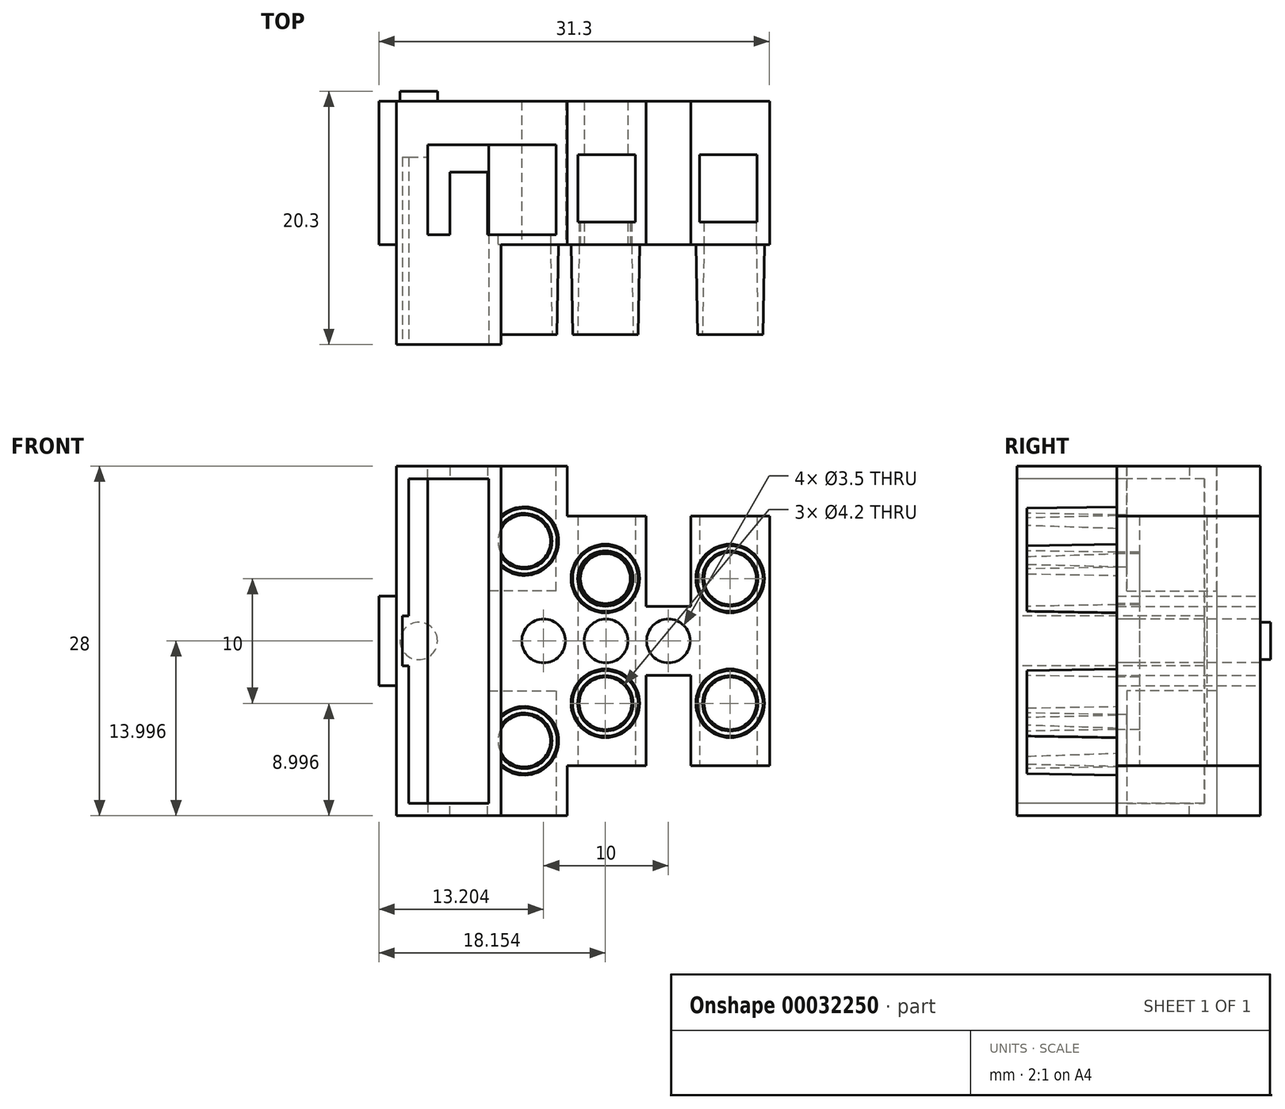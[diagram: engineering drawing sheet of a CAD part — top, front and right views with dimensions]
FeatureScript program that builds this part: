
annotation { "Feature Type Name" : "Feature", "Feature Type Description" : "" }
export const myFeature = defineFeature(function(context is Context, id is Id, definition is map)
    precondition{}
    {
        {
            var Q0;
            Q0=qCreatedBy(makeId("Front.planeOp"),FACE);
            var sketch = newSketch(context, id + "F0", { "sketchPlane" : qUnion([Q0])});
            skLineSegment(sketch, "E0", {"start": v(0.2, 10.65) * mm, "end": v(-6.1, 10.65) * mm});
            skLineSegment(sketch, "E1", {"start": v(-6.1, 10.65) * mm, "end": v(-6.1, 3.4) * mm});
            skLineSegment(sketch, "E2", {"start": v(-6.1, 3.4) * mm, "end": v(-9.7, 3.4) * mm});
            skLineSegment(sketch, "E3", {"start": v(-9.7, 3.4) * mm, "end": v(-9.7, 10.65) * mm});
            skLineSegment(sketch, "E4", {"start": v(-9.7, 10.65) * mm, "end": v(-16, 10.65) * mm});
            skLineSegment(sketch, "E5", {"start": v(0.2, -9.35) * mm, "end": v(-6.1, -9.35) * mm});
            skLineSegment(sketch, "E6", {"start": v(-6.1, -9.35) * mm, "end": v(-6.1, -2.1) * mm});
            skLineSegment(sketch, "E7", {"start": v(-6.1, -2.1) * mm, "end": v(-9.7, -2.1) * mm});
            skLineSegment(sketch, "E8", {"start": v(-9.7, -2.1) * mm, "end": v(-9.7, -9.35) * mm});
            skLineSegment(sketch, "E9", {"start": v(-9.7, -9.35) * mm, "end": v(-16, -9.35) * mm});
            skLineSegment(sketch, "E10", {"start": v(-16, 10.65) * mm, "end": v(-16, 14.65) * mm});
            skLineSegment(sketch, "E11", {"start": v(-16, 14.65) * mm, "end": v(-29.7, 14.65) * mm});
            skLineSegment(sketch, "E12", {"start": v(-29.7, 14.65) * mm, "end": v(-29.7, 4.25) * mm});
            skLineSegment(sketch, "E13", {"start": v(-29.7, -13.35) * mm, "end": v(-16, -13.35) * mm});
            skLineSegment(sketch, "E14", {"start": v(-16, -13.35) * mm, "end": v(-16, -9.35) * mm});
            skLineSegment(sketch, "E15", {"start": v(0.2, 10.65) * mm, "end": v(0.2, -9.35) * mm});
            skLineSegment(sketch, "E16", {"start": v(0.3, 0.65) * mm, "end": v(-43.59, 0.65) * mm, "construction": true});
            skLineSegment(sketch, "E17", {"start": v(-29.7, 4.25) * mm, "end": v(-31.1, 4.25) * mm});
            skLineSegment(sketch, "E18", {"start": v(-31.1, 4.25) * mm, "end": v(-31.1, -2.95) * mm});
            skLineSegment(sketch, "E19", {"start": v(-31.1, -2.95) * mm, "end": v(-29.7, -2.95) * mm});
            skLineSegment(sketch, "E20.trimOffspring", {"start": v(-29.7, -2.95) * mm, "end": v(-29.7, -13.35) * mm});
            skSolve(sketch);
        }
        {
            var Q0;
            Q0 = qSketchRegion(id + "F0", true);
            extrude(context, id + "F1", {"entities" : qUnion([Q0]), "depth" : 11.5 * mm});
        }
        {
            var Q0;
            Q0=makeQuery(id+"F1.opExtrude","CAP_FACE",FACE,{"disambiguationData":[OSD([sQuery(id+"F0.wireOp",EDGE,"E0"),sQuery(id+"F0.wireOp",EDGE,"E1"),sQuery(id+"F0.wireOp",EDGE,"E2"),sQuery(id+"F0.wireOp",EDGE,"E3"),sQuery(id+"F0.wireOp",EDGE,"E4"),sQuery(id+"F0.wireOp",EDGE,"E5"),sQuery(id+"F0.wireOp",EDGE,"E6"),sQuery(id+"F0.wireOp",EDGE,"E7"),sQuery(id+"F0.wireOp",EDGE,"E8"),sQuery(id+"F0.wireOp",EDGE,"E9"),sQuery(id+"F0.wireOp",EDGE,"E10"),sQuery(id+"F0.wireOp",EDGE,"E11"),sQuery(id+"F0.wireOp",EDGE,"E12"),sQuery(id+"F0.wireOp",EDGE,"E13"),sQuery(id+"F0.wireOp",EDGE,"E14"),sQuery(id+"F0.wireOp",EDGE,"E15")])],"isStart":false});
            var sketch = newSketch(context, id + "F2", { "sketchPlane" : qUnion([Q0])});
            skLineSegment(sketch, "E21", {"start": v(0.2, -0.45) * mm, "end": v(-41.93, -0.45) * mm, "construction": true});
            skSolve(sketch);
        }
        {
            var Q0;
            Q0=makeQuery(id+"F2.imprint","IMPRINT",FACE,{"disambiguationData":[TD([[makeQuery(id+"F2.imprint","IMPRINT",EDGE,{"derivedFrom":makeQuery(id+"F1.opExtrude","CAP_EDGE",EDGE,{"disambiguationData":[OSD([sQuery(id+"F0.wireOp",EDGE,"E0")])],"isStart":false})}),1.0]])]});
            var sketch = newSketch(context, id + "F3", { "sketchPlane" : qUnion([Q0])});
            skCircle(sketch, "E22", {"center": v(-2.96, 5.65) * mm, "radius": 2.1 * mm});
            skCircle(sketch, "E23", {"center": v(-2.96, -4.35) * mm, "radius": 2.1 * mm});
            skCircle(sketch, "E24", {"center": v(-12.96, 5.65) * mm, "radius": 2.1 * mm});
            skCircle(sketch, "E25", {"center": v(-12.96, -4.35) * mm, "radius": 2.1 * mm});
            skCircle(sketch, "E26", {"center": v(-19.46, 8.65) * mm, "radius": 2.1 * mm});
            skCircle(sketch, "E27", {"center": v(-19.46, -7.35) * mm, "radius": 2.1 * mm});
            skCircle(sketch, "E28", {"center": v(-2.96, 5.65) * mm, "radius": 2.75 * mm});
            skCircle(sketch, "E29", {"center": v(-2.96, -4.35) * mm, "radius": 2.75 * mm});
            skCircle(sketch, "E30", {"center": v(-12.96, 5.65) * mm, "radius": 2.75 * mm});
            skCircle(sketch, "E31", {"center": v(-12.96, -4.35) * mm, "radius": 2.75 * mm});
            skCircle(sketch, "E32", {"center": v(-19.46, -7.35) * mm, "radius": 2.75 * mm});
            skCircle(sketch, "E33", {"center": v(-19.46, 8.65) * mm, "radius": 2.75 * mm});
            skSolve(sketch);
        }
        {
            var Q0;
            Q0 = qSketchRegion(id + "F3", true);
            extrude(context, id + "F4", {"entities" : qUnion([Q0]), "operationType" : NewBodyOperationType.ADD, "depth" : 7.2 * mm, "hasDraft" : true, "draftAngle" : 1 * degree, "draftPullDirection" : true});
        }
        {
            var Q0;
            Q0=makeQuery(id+"F2.imprint","IMPRINT",FACE,{"disambiguationData":[TD([[makeQuery(id+"F2.imprint","IMPRINT",EDGE,{"derivedFrom":makeQuery(id+"F1.opExtrude","CAP_EDGE",EDGE,{"disambiguationData":[OSD([sQuery(id+"F0.wireOp",EDGE,"E0")])],"isStart":false})}),1.0]])]});
            var sketch = newSketch(context, id + "F5", { "sketchPlane" : qUnion([Q0])});
            skLineSegment(sketch, "E34.bottom", {"start": v(-29.7, 14.65) * mm, "end": v(-21.3, 14.65) * mm});
            skLineSegment(sketch, "E34.top", {"start": v(-29.7, -13.35) * mm, "end": v(-21.3, -13.35) * mm});
            skLineSegment(sketch, "E34.left", {"start": v(-29.7, 14.65) * mm, "end": v(-29.7, -13.35) * mm});
            skLineSegment(sketch, "E34.right", {"start": v(-21.3, 14.65) * mm, "end": v(-21.3, -13.35) * mm});
            skSolve(sketch);
        }
        {
            var Q0;
            Q0 = qSketchRegion(id + "F5", true);
            extrude(context, id + "F6", {"entities" : qUnion([Q0]), "operationType" : NewBodyOperationType.ADD, "depth" : 8 * mm});
        }
        {
            var Q0;
            Q0=makeQuery(id+"F6.opExtrude","CAP_FACE",FACE,{"disambiguationData":[OSD([sQuery(id+"F5.wireOp",EDGE,"E34.bottom"),sQuery(id+"F5.wireOp",EDGE,"E34.top"),sQuery(id+"F5.wireOp",EDGE,"E34.left"),sQuery(id+"F5.wireOp",EDGE,"E34.right")])],"isStart":false});
            var sketch = newSketch(context, id + "F7", { "sketchPlane" : qUnion([Q0])});
            skLineSegment(sketch, "E35.bottom", {"start": v(-28.7, 13.65) * mm, "end": v(-22.3, 13.65) * mm});
            skLineSegment(sketch, "E35.top", {"start": v(-28.7, -12.35) * mm, "end": v(-22.3, -12.35) * mm});
            skLineSegment(sketch, "E35.right", {"start": v(-22.3, 13.65) * mm, "end": v(-22.3, -12.35) * mm});
            skLineSegment(sketch, "E36", {"start": v(-28.7, -12.35) * mm, "end": v(-28.7, -1.35) * mm});
            skLineSegment(sketch, "E37", {"start": v(-28.7, -1.35) * mm, "end": v(-29.2, -1.35) * mm});
            skLineSegment(sketch, "E38", {"start": v(-29.2, -1.35) * mm, "end": v(-29.2, 2.65) * mm});
            skLineSegment(sketch, "E39", {"start": v(-29.2, 2.65) * mm, "end": v(-28.7, 2.65) * mm});
            skLineSegment(sketch, "E40", {"start": v(-28.7, 2.65) * mm, "end": v(-28.7, 13.65) * mm});
            skLineSegment(sketch, "E41", {"start": v(-22.3, 0.65) * mm, "end": v(-29.2, 0.65) * mm, "construction": true});
            skPoint(sketch, "E41.endSnap0", {"position": v(-29.7, 0.65) * mm});
            skSolve(sketch);
        }
        {
            var Q0;
            Q0 = qSketchRegion(id + "F7", true);
            extrude(context, id + "F8", {"entities" : qUnion([Q0]), "operationType" : NewBodyOperationType.REMOVE, "oppositeDirection" : true, "depth" : 15 * mm});
        }
        {
            var Q0;
            Q0=makeQuery(id+"F2.imprint","IMPRINT",FACE,{"disambiguationData":[TD([[makeQuery(id+"F2.imprint","IMPRINT",EDGE,{"derivedFrom":makeQuery(id+"F1.opExtrude","CAP_EDGE",EDGE,{"disambiguationData":[OSD([sQuery(id+"F0.wireOp",EDGE,"E0")])],"isStart":false})}),1.0]])]});
            var sketch = newSketch(context, id + "F9", { "sketchPlane" : qUnion([Q0])});
            skCircle(sketch, "E42", {"center": v(-7.9, 0.65) * mm, "radius": 1.75 * mm});
            skCircle(sketch, "E43", {"center": v(-12.9, 0.65) * mm, "radius": 1.75 * mm});
            skCircle(sketch, "E44", {"center": v(-17.9, 0.65) * mm, "radius": 1.75 * mm});
            skSolve(sketch);
        }
        {
            var Q0;
            Q0=makeQuery(id+"F1.opExtrude","SWEPT_FACE",FACE,{"disambiguationData":[OSD([sQuery(id+"F0.wireOp",EDGE,"E5")])]});
            var sketch = newSketch(context, id + "F10", { "sketchPlane" : qUnion([Q0])});
            skLineSegment(sketch, "E45.bottom", {"start": v(-5.4, 9.7) * mm, "end": v(-0.8, 9.7) * mm});
            skLineSegment(sketch, "E45.top", {"start": v(-5.4, 4.3) * mm, "end": v(-0.8, 4.3) * mm});
            skLineSegment(sketch, "E45.left", {"start": v(-5.4, 9.7) * mm, "end": v(-5.4, 4.3) * mm});
            skLineSegment(sketch, "E45.right", {"start": v(-0.8, 9.7) * mm, "end": v(-0.8, 4.3) * mm});
            skLineSegment(sketch, "E46.bottom", {"start": v(-15.16, 9.7) * mm, "end": v(-10.56, 9.7) * mm});
            skLineSegment(sketch, "E46.top", {"start": v(-15.16, 4.3) * mm, "end": v(-10.56, 4.3) * mm});
            skLineSegment(sketch, "E46.left", {"start": v(-15.16, 9.7) * mm, "end": v(-15.16, 4.3) * mm});
            skLineSegment(sketch, "E46.right", {"start": v(-10.56, 9.7) * mm, "end": v(-10.56, 4.3) * mm});
            skSolve(sketch);
        }
        {
            var Q0;
            Q0 = qSketchRegion(id + "F10", true);
            extrude(context, id + "F11", {"entities" : qUnion([Q0]), "operationType" : NewBodyOperationType.REMOVE, "endBound" : BoundingType.UP_TO_NEXT, "oppositeDirection" : true, "depth" : 25 * mm});
        }
        {
            var Q0;
            Q0=makeQuery(id+"F6.boolean.opBoolean","MERGE",FACE,{"derivedFrom":[makeQuery(id+"F1.opExtrude","SWEPT_FACE",FACE,{"disambiguationData":[OSD([sQuery(id+"F0.wireOp",EDGE,"E13")])]}),makeQuery(id+"F6.opExtrude","SWEPT_FACE",FACE,{"disambiguationData":[OSD([sQuery(id+"F5.wireOp",EDGE,"E34.top")])]})]});
            var sketch = newSketch(context, id + "F12", { "sketchPlane" : qUnion([Q0])});
            skLineSegment(sketch, "E47.bottom", {"start": v(-27.2, 10.7) * mm, "end": v(-16.9, 10.7) * mm});
            skLineSegment(sketch, "E47.top", {"start": v(-27.2, 3.5) * mm, "end": v(-16.9, 3.5) * mm});
            skLineSegment(sketch, "E47.left", {"start": v(-27.2, 10.7) * mm, "end": v(-27.2, 3.5) * mm});
            skLineSegment(sketch, "E47.right", {"start": v(-16.9, 10.7) * mm, "end": v(-16.9, 3.5) * mm});
            skSolve(sketch);
        }
        {
            var Q0;
            Q0 = qSketchRegion(id + "F12", true);
            var Q1;
            Q1=makeQuery(id+"F6.boolean.opBoolean","MERGE",FACE,{"derivedFrom":[makeQuery(id+"F1.opExtrude","SWEPT_FACE",FACE,{"disambiguationData":[OSD([sQuery(id+"F0.wireOp",EDGE,"E11")])]}),makeQuery(id+"F6.opExtrude","SWEPT_FACE",FACE,{"disambiguationData":[OSD([sQuery(id+"F5.wireOp",EDGE,"E34.bottom")])]})]});
            extrude(context, id + "F13", {"entities" : qUnion([Q0]), "operationType" : NewBodyOperationType.REMOVE, "oppositeDirection" : true, "endBoundEntityFace" : qUnion([Q1]), "depth" : 10 * mm});
        }
        {
            var Q0;
            Q0=makeQuery(id+"F4.boolean.opBoolean","SPLIT",FACE,{"disambiguationData":[TD([makeQuery(id+"F4.opExtrude","SWEPT_FACE",FACE,{"disambiguationData":[OSD([sQuery(id+"F3.wireOp",EDGE,"E24")])]})])],"derivedFrom":makeQuery(id+"F1.opExtrude","CAP_FACE",FACE,{"disambiguationData":[OSD([sQuery(id+"F0.wireOp",EDGE,"E0"),sQuery(id+"F0.wireOp",EDGE,"E1"),sQuery(id+"F0.wireOp",EDGE,"E2"),sQuery(id+"F0.wireOp",EDGE,"E3"),sQuery(id+"F0.wireOp",EDGE,"E4"),sQuery(id+"F0.wireOp",EDGE,"E5"),sQuery(id+"F0.wireOp",EDGE,"E6"),sQuery(id+"F0.wireOp",EDGE,"E7"),sQuery(id+"F0.wireOp",EDGE,"E8"),sQuery(id+"F0.wireOp",EDGE,"E9"),sQuery(id+"F0.wireOp",EDGE,"E10"),sQuery(id+"F0.wireOp",EDGE,"E11"),sQuery(id+"F0.wireOp",EDGE,"E12"),sQuery(id+"F0.wireOp",EDGE,"E13"),sQuery(id+"F0.wireOp",EDGE,"E14"),sQuery(id+"F0.wireOp",EDGE,"E15")])],"isStart":false})});
            var sketch = newSketch(context, id + "F14", { "sketchPlane" : qUnion([Q0])});
            skCircle(sketch, "E48", {"center": v(-12.96, 5.65) * mm, "radius": 2 * mm});
            skSolve(sketch);
        }
        {
            var Q0;
            Q0 = qSketchRegion(id + "F14", true);
            var Q1;
            Q1=makeQuery(id+"F11.boolean.opBoolean","COPY",FACE,{"derivedFrom":makeQuery(id+"F11.opExtrude","SWEPT_FACE",FACE,{"disambiguationData":[OSD([sQuery(id+"F10.wireOp",EDGE,"E46.bottom")])]})});
            extrude(context, id + "F15", {"entities" : qUnion([Q0]), "operationType" : NewBodyOperationType.REMOVE, "oppositeDirection" : true, "endBoundEntityFace" : qUnion([Q1]), "depth" : 2 * mm});
        }
        {
            var Q0;
            Q0=makeQuery(id+"F4.boolean.opBoolean","SPLIT",FACE,{"disambiguationData":[TD([makeQuery(id+"F4.opExtrude","SWEPT_FACE",FACE,{"disambiguationData":[OSD([sQuery(id+"F3.wireOp",EDGE,"E25")])]})])],"derivedFrom":makeQuery(id+"F1.opExtrude","CAP_FACE",FACE,{"disambiguationData":[OSD([sQuery(id+"F0.wireOp",EDGE,"E0"),sQuery(id+"F0.wireOp",EDGE,"E1"),sQuery(id+"F0.wireOp",EDGE,"E2"),sQuery(id+"F0.wireOp",EDGE,"E3"),sQuery(id+"F0.wireOp",EDGE,"E4"),sQuery(id+"F0.wireOp",EDGE,"E5"),sQuery(id+"F0.wireOp",EDGE,"E6"),sQuery(id+"F0.wireOp",EDGE,"E7"),sQuery(id+"F0.wireOp",EDGE,"E8"),sQuery(id+"F0.wireOp",EDGE,"E9"),sQuery(id+"F0.wireOp",EDGE,"E10"),sQuery(id+"F0.wireOp",EDGE,"E11"),sQuery(id+"F0.wireOp",EDGE,"E12"),sQuery(id+"F0.wireOp",EDGE,"E13"),sQuery(id+"F0.wireOp",EDGE,"E14"),sQuery(id+"F0.wireOp",EDGE,"E15")])],"isStart":false})});
            var sketch = newSketch(context, id + "F16", { "sketchPlane" : qUnion([Q0])});
            skCircle(sketch, "E49", {"center": v(-12.96, -4.35) * mm, "radius": 2.1 * mm});
            skPoint(sketch, "E49.first.point", {"position": v(-12.64, -2.28) * mm});
            skPoint(sketch, "E49.second.point", {"position": v(-10.86, -4.3) * mm});
            skPoint(sketch, "E49.third.point", {"position": v(-14.75, -3.26) * mm});
            skSolve(sketch);
        }
        {
            var Q0;
            Q0 = qSketchRegion(id + "F16", true);
            extrude(context, id + "F17", {"entities" : qUnion([Q0]), "operationType" : NewBodyOperationType.REMOVE, "oppositeDirection" : true, "depth" : 2 * mm});
        }
        {
            var Q0;
            Q0=makeQuery(id+"F4.boolean.opBoolean","SPLIT",FACE,{"disambiguationData":[TD([makeQuery(id+"F4.opExtrude","SWEPT_FACE",FACE,{"disambiguationData":[OSD([sQuery(id+"F3.wireOp",EDGE,"E22")])]})])],"derivedFrom":makeQuery(id+"F1.opExtrude","CAP_FACE",FACE,{"disambiguationData":[OSD([sQuery(id+"F0.wireOp",EDGE,"E0"),sQuery(id+"F0.wireOp",EDGE,"E1"),sQuery(id+"F0.wireOp",EDGE,"E2"),sQuery(id+"F0.wireOp",EDGE,"E3"),sQuery(id+"F0.wireOp",EDGE,"E4"),sQuery(id+"F0.wireOp",EDGE,"E5"),sQuery(id+"F0.wireOp",EDGE,"E6"),sQuery(id+"F0.wireOp",EDGE,"E7"),sQuery(id+"F0.wireOp",EDGE,"E8"),sQuery(id+"F0.wireOp",EDGE,"E9"),sQuery(id+"F0.wireOp",EDGE,"E10"),sQuery(id+"F0.wireOp",EDGE,"E11"),sQuery(id+"F0.wireOp",EDGE,"E12"),sQuery(id+"F0.wireOp",EDGE,"E13"),sQuery(id+"F0.wireOp",EDGE,"E14"),sQuery(id+"F0.wireOp",EDGE,"E15")])],"isStart":false})});
            var sketch = newSketch(context, id + "F18", { "sketchPlane" : qUnion([Q0])});
            skCircle(sketch, "E50", {"center": v(-2.96, 5.65) * mm, "radius": 2.1 * mm});
            skPoint(sketch, "E50.first.point", {"position": v(-1.2, 4.5) * mm});
            skPoint(sketch, "E50.second.point", {"position": v(-1.2, 4.5) * mm});
            skPoint(sketch, "E50.third.point", {"position": v(-4.91, 6.41) * mm});
            skSolve(sketch);
        }
        {
            var Q0;
            Q0 = qSketchRegion(id + "F18", true);
            extrude(context, id + "F19", {"entities" : qUnion([Q0]), "operationType" : NewBodyOperationType.REMOVE, "oppositeDirection" : true, "depth" : 2 * mm});
        }
        {
            var Q0;
            Q0=makeQuery(id+"F4.boolean.opBoolean","SPLIT",FACE,{"disambiguationData":[TD([makeQuery(id+"F4.opExtrude","SWEPT_FACE",FACE,{"disambiguationData":[OSD([sQuery(id+"F3.wireOp",EDGE,"E23")])]})])],"derivedFrom":makeQuery(id+"F1.opExtrude","CAP_FACE",FACE,{"disambiguationData":[OSD([sQuery(id+"F0.wireOp",EDGE,"E0"),sQuery(id+"F0.wireOp",EDGE,"E1"),sQuery(id+"F0.wireOp",EDGE,"E2"),sQuery(id+"F0.wireOp",EDGE,"E3"),sQuery(id+"F0.wireOp",EDGE,"E4"),sQuery(id+"F0.wireOp",EDGE,"E5"),sQuery(id+"F0.wireOp",EDGE,"E6"),sQuery(id+"F0.wireOp",EDGE,"E7"),sQuery(id+"F0.wireOp",EDGE,"E8"),sQuery(id+"F0.wireOp",EDGE,"E9"),sQuery(id+"F0.wireOp",EDGE,"E10"),sQuery(id+"F0.wireOp",EDGE,"E11"),sQuery(id+"F0.wireOp",EDGE,"E12"),sQuery(id+"F0.wireOp",EDGE,"E13"),sQuery(id+"F0.wireOp",EDGE,"E14"),sQuery(id+"F0.wireOp",EDGE,"E15")])],"isStart":false})});
            var sketch = newSketch(context, id + "F20", { "sketchPlane" : qUnion([Q0])});
            skCircle(sketch, "E51", {"center": v(-2.96, -4.35) * mm, "radius": 2.1 * mm});
            skPoint(sketch, "E51.first.point", {"position": v(-4.29, -2.73) * mm});
            skPoint(sketch, "E51.second.point", {"position": v(-1.8, -2.6) * mm});
            skPoint(sketch, "E51.third.point", {"position": v(-1.13, -5.39) * mm});
            skSolve(sketch);
        }
        {
            var Q0;
            Q0 = qSketchRegion(id + "F20", true);
            extrude(context, id + "F21", {"entities" : qUnion([Q0]), "operationType" : NewBodyOperationType.REMOVE, "oppositeDirection" : true, "depth" : 2 * mm});
        }
        {
            var Q0;
            Q0=makeQuery(id+"F4.boolean.opBoolean","SPLIT",FACE,{"disambiguationData":[TD([makeQuery(id+"F4.opExtrude","SWEPT_FACE",FACE,{"disambiguationData":[OSD([sQuery(id+"F3.wireOp",EDGE,"E26")])]})])],"derivedFrom":makeQuery(id+"F1.opExtrude","CAP_FACE",FACE,{"disambiguationData":[OSD([sQuery(id+"F0.wireOp",EDGE,"E0"),sQuery(id+"F0.wireOp",EDGE,"E1"),sQuery(id+"F0.wireOp",EDGE,"E2"),sQuery(id+"F0.wireOp",EDGE,"E3"),sQuery(id+"F0.wireOp",EDGE,"E4"),sQuery(id+"F0.wireOp",EDGE,"E5"),sQuery(id+"F0.wireOp",EDGE,"E6"),sQuery(id+"F0.wireOp",EDGE,"E7"),sQuery(id+"F0.wireOp",EDGE,"E8"),sQuery(id+"F0.wireOp",EDGE,"E9"),sQuery(id+"F0.wireOp",EDGE,"E10"),sQuery(id+"F0.wireOp",EDGE,"E11"),sQuery(id+"F0.wireOp",EDGE,"E12"),sQuery(id+"F0.wireOp",EDGE,"E13"),sQuery(id+"F0.wireOp",EDGE,"E14"),sQuery(id+"F0.wireOp",EDGE,"E15")])],"isStart":false})});
            var sketch = newSketch(context, id + "F22", { "sketchPlane" : qUnion([Q0])});
            skCircle(sketch, "E52", {"center": v(-19.46, 8.65) * mm, "radius": 2.1 * mm});
            skPoint(sketch, "E52.first.point", {"position": v(-20.56, 10.43) * mm});
            skPoint(sketch, "E52.second.point", {"position": v(-18.21, 10.34) * mm});
            skPoint(sketch, "E52.third.point", {"position": v(-17.5, 7.87) * mm});
            skSolve(sketch);
        }
        {
            var Q0;
            Q0 = qSketchRegion(id + "F22", true);
            extrude(context, id + "F23", {"entities" : qUnion([Q0]), "operationType" : NewBodyOperationType.REMOVE, "oppositeDirection" : true, "depth" : 2 * mm});
        }
        {
            var Q0;
            Q0=makeQuery(id+"F4.boolean.opBoolean","SPLIT",FACE,{"disambiguationData":[TD([makeQuery(id+"F4.opExtrude","SWEPT_FACE",FACE,{"disambiguationData":[OSD([sQuery(id+"F3.wireOp",EDGE,"E27")])]})])],"derivedFrom":makeQuery(id+"F1.opExtrude","CAP_FACE",FACE,{"disambiguationData":[OSD([sQuery(id+"F0.wireOp",EDGE,"E0"),sQuery(id+"F0.wireOp",EDGE,"E1"),sQuery(id+"F0.wireOp",EDGE,"E2"),sQuery(id+"F0.wireOp",EDGE,"E3"),sQuery(id+"F0.wireOp",EDGE,"E4"),sQuery(id+"F0.wireOp",EDGE,"E5"),sQuery(id+"F0.wireOp",EDGE,"E6"),sQuery(id+"F0.wireOp",EDGE,"E7"),sQuery(id+"F0.wireOp",EDGE,"E8"),sQuery(id+"F0.wireOp",EDGE,"E9"),sQuery(id+"F0.wireOp",EDGE,"E10"),sQuery(id+"F0.wireOp",EDGE,"E11"),sQuery(id+"F0.wireOp",EDGE,"E12"),sQuery(id+"F0.wireOp",EDGE,"E13"),sQuery(id+"F0.wireOp",EDGE,"E14"),sQuery(id+"F0.wireOp",EDGE,"E15")])],"isStart":false})});
            var sketch = newSketch(context, id + "F24", { "sketchPlane" : qUnion([Q0])});
            skCircle(sketch, "E53", {"center": v(-19.46, -7.35) * mm, "radius": 2.1 * mm});
            skPoint(sketch, "E53.first.point", {"position": v(-20.48, -5.52) * mm});
            skPoint(sketch, "E53.second.point", {"position": v(-17.44, -6.77) * mm});
            skPoint(sketch, "E53.third.point", {"position": v(-18.33, -9.13) * mm});
            skSolve(sketch);
        }
        {
            var Q0;
            Q0 = qSketchRegion(id + "F24", true);
            extrude(context, id + "F25", {"entities" : qUnion([Q0]), "operationType" : NewBodyOperationType.REMOVE, "oppositeDirection" : true, "depth" : 2 * mm});
        }
        {
            var Q0;
            Q0=makeQuery(id+"F6.boolean.opBoolean","MERGE",FACE,{"derivedFrom":[makeQuery(id+"F1.opExtrude","SWEPT_FACE",FACE,{"disambiguationData":[OSD([sQuery(id+"F0.wireOp",EDGE,"E11")])]}),makeQuery(id+"F6.opExtrude","SWEPT_FACE",FACE,{"disambiguationData":[OSD([sQuery(id+"F5.wireOp",EDGE,"E34.bottom")])]})]});
            var sketch = newSketch(context, id + "F26", { "sketchPlane" : qUnion([Q0])});
            skLineSegment(sketch, "E54.bottom", {"start": v(-16.9, -10.7) * mm, "end": v(-27.2, -10.7) * mm});
            skLineSegment(sketch, "E54.top", {"start": v(-16.9, -3.5) * mm, "end": v(-27.2, -3.5) * mm});
            skLineSegment(sketch, "E54.left", {"start": v(-16.9, -10.7) * mm, "end": v(-16.9, -3.5) * mm});
            skLineSegment(sketch, "E54.right", {"start": v(-27.2, -10.7) * mm, "end": v(-27.2, -3.5) * mm});
            skSolve(sketch);
        }
        {
            var Q0;
            Q0 = qSketchRegion(id + "F26", true);
            extrude(context, id + "F27", {"entities" : qUnion([Q0]), "operationType" : NewBodyOperationType.REMOVE, "oppositeDirection" : true, "depth" : 10 * mm});
        }
        {
            var Q0;
            Q0 = qSketchRegion(id + "F9", true);
            extrude(context, id + "F28", {"entities" : qUnion([Q0]), "operationType" : NewBodyOperationType.REMOVE, "oppositeDirection" : true, "depth" : 12 * mm});
        }
        {
            var Q0;
            Q0=makeQuery(id+"F1.opExtrude","CAP_FACE",FACE,{"disambiguationData":[OSD([sQuery(id+"F0.wireOp",EDGE,"E0"),sQuery(id+"F0.wireOp",EDGE,"E1"),sQuery(id+"F0.wireOp",EDGE,"E2"),sQuery(id+"F0.wireOp",EDGE,"E3"),sQuery(id+"F0.wireOp",EDGE,"E4"),sQuery(id+"F0.wireOp",EDGE,"E5"),sQuery(id+"F0.wireOp",EDGE,"E6"),sQuery(id+"F0.wireOp",EDGE,"E7"),sQuery(id+"F0.wireOp",EDGE,"E8"),sQuery(id+"F0.wireOp",EDGE,"E9"),sQuery(id+"F0.wireOp",EDGE,"E10"),sQuery(id+"F0.wireOp",EDGE,"E11"),sQuery(id+"F0.wireOp",EDGE,"E12"),sQuery(id+"F0.wireOp",EDGE,"E13"),sQuery(id+"F0.wireOp",EDGE,"E14"),sQuery(id+"F0.wireOp",EDGE,"E15"),sQuery(id+"F0.wireOp",EDGE,"E17"),sQuery(id+"F0.wireOp",EDGE,"E18"),sQuery(id+"F0.wireOp",EDGE,"E19"),sQuery(id+"F0.wireOp",EDGE,"E20.trimOffspring")])],"isStart":true});
            var sketch = newSketch(context, id + "F29", { "sketchPlane" : qUnion([Q0])});
            skCircle(sketch, "E55", {"center": v(27.9, 0.65) * mm, "radius": 1.5 * mm});
            skSolve(sketch);
        }
        {
            var Q0;
            Q0 = qSketchRegion(id + "F29", true);
            extrude(context, id + "F30", {"entities" : qUnion([Q0]), "operationType" : NewBodyOperationType.ADD, "depth" : 0.8 * mm});
        }
        {
            var Q0;
            Q0=makeQuery(id+"F8.boolean.opBoolean","COPY",FACE,{"derivedFrom":makeQuery(id+"F8.opExtrude","CAP_FACE",FACE,{"disambiguationData":[OSD([sQuery(id+"F7.wireOp",EDGE,"E35.bottom"),sQuery(id+"F7.wireOp",EDGE,"E35.top"),sQuery(id+"F7.wireOp",EDGE,"E35.right"),sQuery(id+"F7.wireOp",EDGE,"E36"),sQuery(id+"F7.wireOp",EDGE,"E37"),sQuery(id+"F7.wireOp",EDGE,"E38"),sQuery(id+"F7.wireOp",EDGE,"E39"),sQuery(id+"F7.wireOp",EDGE,"E40")])],"isStart":false})});
            var sketch = newSketch(context, id + "F31", { "sketchPlane" : qUnion([Q0])});
            skLineSegment(sketch, "E56.bottom", {"start": v(-27.2, 4.65) * mm, "end": v(-22.3, 4.65) * mm});
            skLineSegment(sketch, "E56.top", {"start": v(-27.2, -3.35) * mm, "end": v(-22.3, -3.35) * mm});
            skLineSegment(sketch, "E56.left", {"start": v(-27.2, 4.65) * mm, "end": v(-27.2, -3.35) * mm});
            skLineSegment(sketch, "E56.right", {"start": v(-22.3, 4.65) * mm, "end": v(-22.3, -3.35) * mm});
            skSolve(sketch);
        }
        {
            var Q0;
            Q0=makeQuery(id+"F31.imprint","IMPRINT",FACE,{"disambiguationData":[TD([[makeQuery(id+"F31.imprint","IMPRINT",EDGE,{"derivedFrom":sQuery(id+"F31.wireOp",EDGE,"E56.bottom")}),1.0]])]});
            var Q1;
            Q1=makeQuery(id+"F13.boolean.opBoolean","COPY",FACE,{"derivedFrom":makeQuery(id+"F13.opExtrude","SWEPT_FACE",FACE,{"disambiguationData":[OSD([sQuery(id+"F12.wireOp",EDGE,"E47.top")])]})});
            extrude(context, id + "F32", {"entities" : qUnion([Q0]), "operationType" : NewBodyOperationType.REMOVE, "endBound" : BoundingType.UP_TO_SURFACE, "oppositeDirection" : true, "endBoundEntityFace" : qUnion([Q1]), "depth" : 25 * mm});
        }
        {
            var Q0;
            Q0=makeQuery(id+"F13.boolean.opBoolean","COPY",FACE,{"derivedFrom":makeQuery(id+"F13.opExtrude","SWEPT_FACE",FACE,{"disambiguationData":[OSD([sQuery(id+"F12.wireOp",EDGE,"E47.bottom")])]})});
            var sketch = newSketch(context, id + "F33", { "sketchPlane" : qUnion([Q0])});
            skLineSegment(sketch, "E57.bottom", {"start": v(25.4, -13.35) * mm, "end": v(22.4, -13.35) * mm});
            skLineSegment(sketch, "E57.top", {"start": v(25.4, -12.35) * mm, "end": v(22.4, -12.35) * mm});
            skLineSegment(sketch, "E57.left", {"start": v(25.4, -13.35) * mm, "end": v(25.4, -12.35) * mm});
            skLineSegment(sketch, "E57.right", {"start": v(22.4, -13.35) * mm, "end": v(22.4, -12.35) * mm});
            skSolve(sketch);
        }
        {
            var Q0;
            Q0 = qSketchRegion(id + "F33", true);
            extrude(context, id + "F34", {"entities" : qUnion([Q0]), "operationType" : NewBodyOperationType.ADD, "depth" : 5 * mm});
        }
        {
            var Q0;
            Q0=makeQuery(id+"F27.boolean.opBoolean","COPY",FACE,{"derivedFrom":makeQuery(id+"F27.opExtrude","SWEPT_FACE",FACE,{"disambiguationData":[OSD([sQuery(id+"F26.wireOp",EDGE,"E54.bottom")])]})});
            var sketch = newSketch(context, id + "F35", { "sketchPlane" : qUnion([Q0])});
            skLineSegment(sketch, "E58.bottom", {"start": v(25.4, 14.65) * mm, "end": v(22.4, 14.65) * mm});
            skLineSegment(sketch, "E58.top", {"start": v(25.4, 13.65) * mm, "end": v(22.4, 13.65) * mm});
            skLineSegment(sketch, "E58.left", {"start": v(25.4, 14.65) * mm, "end": v(25.4, 13.65) * mm});
            skLineSegment(sketch, "E58.right", {"start": v(22.4, 14.65) * mm, "end": v(22.4, 13.65) * mm});
            skSolve(sketch);
        }
        {
            var Q0;
            Q0 = qSketchRegion(id + "F35", true);
            extrude(context, id + "F36", {"entities" : qUnion([Q0]), "operationType" : NewBodyOperationType.ADD, "depth" : 5 * mm});
        }
    });
